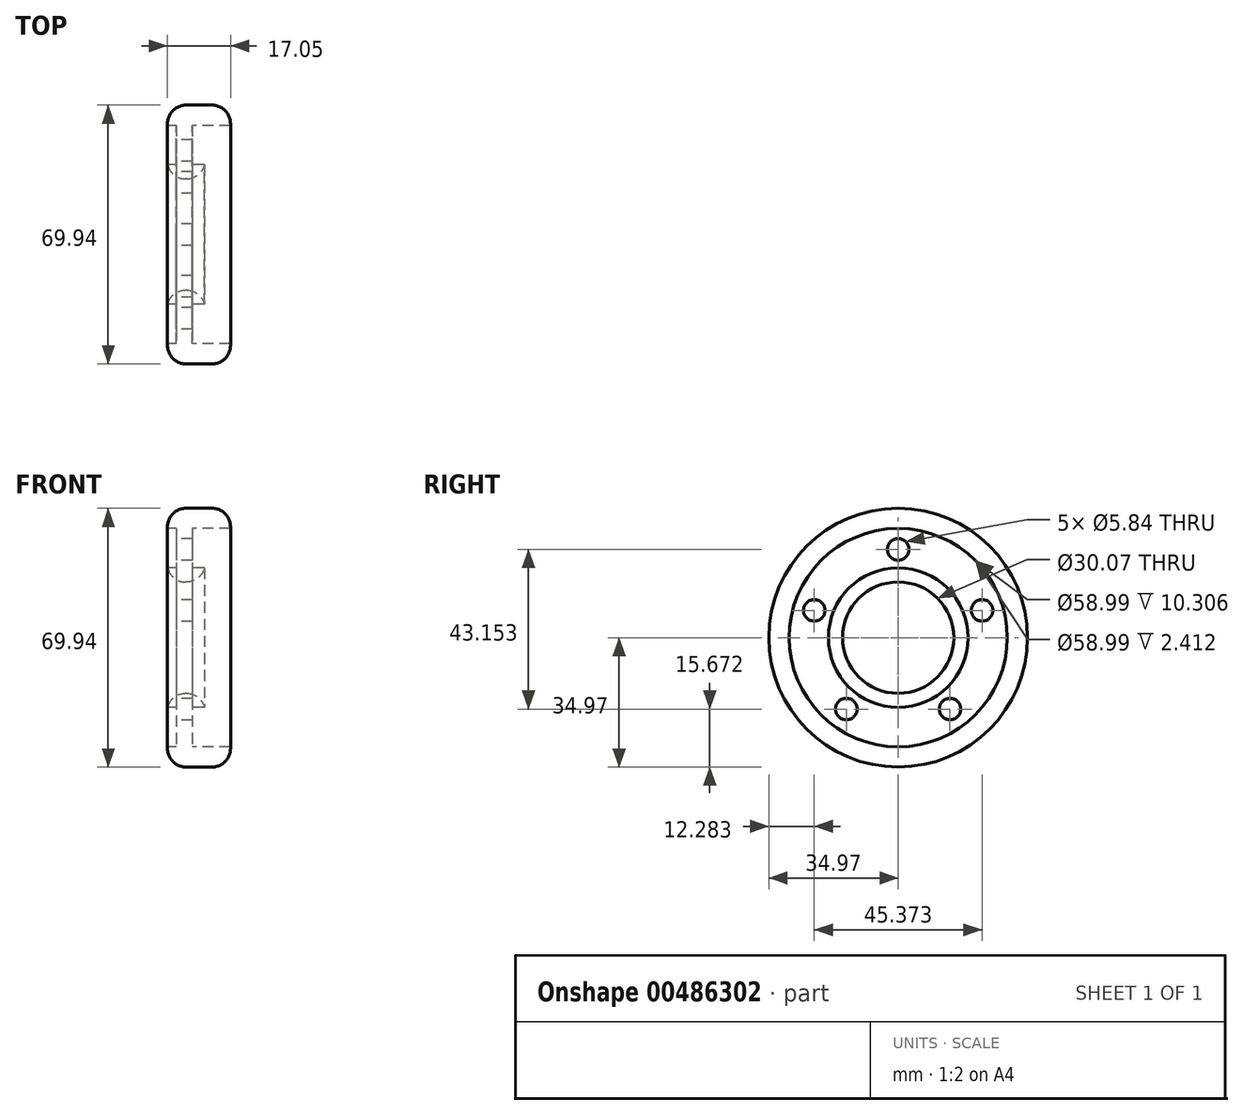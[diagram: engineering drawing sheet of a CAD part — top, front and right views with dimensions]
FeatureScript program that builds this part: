
annotation { "Feature Type Name" : "Feature", "Feature Type Description" : "" }
export const myFeature = defineFeature(function(context is Context, id is Id, definition is map)
    precondition{}
    {
        {
            var Q0;
            Q0=qCreatedBy(makeId("Front.planeOp"),FACE);
            var sketch = newSketch(context, id + "F0", { "sketchPlane" : qUnion([Q0])});
            skLineSegment(sketch, "E0", {"start": v(0, 15.04) * mm, "end": v(10, 15.04) * mm});
            skLineSegment(sketch, "E1", {"start": v(10, 15.04) * mm, "end": v(10, 18.87) * mm});
            skLineSegment(sketch, "E2", {"start": v(10, 18.87) * mm, "end": v(6.75, 18.87) * mm});
            skLineSegment(sketch, "E3", {"start": v(6.75, 18.87) * mm, "end": v(6.75, 29.5) * mm});
            skLineSegment(sketch, "E4", {"start": v(6.75, 29.5) * mm, "end": v(17.05, 29.5) * mm});
            skLineSegment(sketch, "E5", {"start": v(17.05, 29.5) * mm, "end": v(17.05, 34.97) * mm});
            skLineSegment(sketch, "E6", {"start": v(17.05, 34.97) * mm, "end": v(0, 34.97) * mm});
            skLineSegment(sketch, "E7", {"start": v(0, 34.97) * mm, "end": v(0, 29.5) * mm});
            skLineSegment(sketch, "E8", {"start": v(0, 29.5) * mm, "end": v(2.41, 29.5) * mm});
            skLineSegment(sketch, "E9", {"start": v(2.41, 29.5) * mm, "end": v(2.41, 18.87) * mm});
            skLineSegment(sketch, "E10", {"start": v(2.41, 18.87) * mm, "end": v(0, 18.87) * mm});
            skLineSegment(sketch, "E11", {"start": v(0, 18.87) * mm, "end": v(0, 15.04) * mm});
            skLineSegment(sketch, "E12", {"start": v(0, 0) * mm, "end": v(12.67, 0) * mm});
            skSolve(sketch);
        }
        {
            var Q0;
            Q0=makeQuery(id+"F0.imprint","IMPRINT",FACE,{"disambiguationData":[TD([[makeQuery(id+"F0.imprint","IMPRINT",EDGE,{"derivedFrom":sQuery(id+"F0.wireOp",EDGE,"E0")}),1.0]])]});
            var Q1;
            Q1=sQuery(id+"F0.wireOp",EDGE,"E12");
            revolve(context, id + "F1", {"entities" : qUnion([Q0]), "axis" : qUnion([Q1]), "revolveType" : RevolveType.FULL});
        }
        {
            var Q0;
            Q0=makeQuery(id+"F1.opRevolve","SWEPT_FACE",FACE,{"disambiguationData":[OSD([sQuery(id+"F0.wireOp",EDGE,"E9")])]});
            var sketch = newSketch(context, id + "F2", { "sketchPlane" : qUnion([Q0])});
            skCircle(sketch, "E13", {"center": v(0, 23.85) * mm, "radius": 2.92 * mm});
            skCircle(sketch, "E14.1.0", {"center": v(-22.69, 7.37) * mm, "radius": 2.92 * mm});
            skCircle(sketch, "E14.2.0", {"center": v(-14.02, -19.3) * mm, "radius": 2.92 * mm});
            skCircle(sketch, "E14.3.0", {"center": v(14.02, -19.3) * mm, "radius": 2.92 * mm});
            skCircle(sketch, "E14.4.0", {"center": v(22.69, 7.37) * mm, "radius": 2.92 * mm});
            skPoint(sketch, "E14.center", {"position": v(0, 0) * mm});
            skSolve(sketch);
        }
        {
            var Q0;
            Q0=makeQuery(id+"F2.imprint","IMPRINT",FACE,{"disambiguationData":[TD([[makeQuery(id+"F2.imprint","IMPRINT",EDGE,{"derivedFrom":sQuery(id+"F2.wireOp",EDGE,"E14.1.0")}),1.0]])]});
            var Q1;
            Q1=makeQuery(id+"F2.imprint","IMPRINT",FACE,{"disambiguationData":[TD([[makeQuery(id+"F2.imprint","IMPRINT",EDGE,{"derivedFrom":sQuery(id+"F2.wireOp",EDGE,"E13")}),1.0]])]});
            var Q2;
            Q2=makeQuery(id+"F2.imprint","IMPRINT",FACE,{"disambiguationData":[TD([[makeQuery(id+"F2.imprint","IMPRINT",EDGE,{"derivedFrom":sQuery(id+"F2.wireOp",EDGE,"E14.4.0")}),1.0]])]});
            var Q3;
            Q3=makeQuery(id+"F2.imprint","IMPRINT",FACE,{"disambiguationData":[TD([[makeQuery(id+"F2.imprint","IMPRINT",EDGE,{"derivedFrom":sQuery(id+"F2.wireOp",EDGE,"E14.3.0")}),1.0]])]});
            var Q4;
            Q4=makeQuery(id+"F2.imprint","IMPRINT",FACE,{"disambiguationData":[TD([[makeQuery(id+"F2.imprint","IMPRINT",EDGE,{"derivedFrom":sQuery(id+"F2.wireOp",EDGE,"E14.2.0")}),1.0]])]});
            extrude(context, id + "F3", {"entities" : qUnion([Q0, Q1, Q2, Q3, Q4]), "operationType" : NewBodyOperationType.REMOVE, "oppositeDirection" : true, "depth" : 25 * mm});
        }
        {
            var Q0;
            Q0=makeQuery(id+"F1.opRevolve","SWEPT_EDGE",EDGE,{"disambiguationData":[OSD([sQuery(id+"F0.wireOp",EDGE,"E6"),sQuery(id+"F0.wireOp",EDGE,"E7")])]});
            var Q1;
            Q1=makeQuery(id+"F1.opRevolve","SWEPT_EDGE",EDGE,{"disambiguationData":[OSD([sQuery(id+"F0.wireOp",EDGE,"E0"),sQuery(id+"F0.wireOp",EDGE,"E11")])]});
            var Q2;
            Q2=makeQuery(id+"F1.opRevolve","SWEPT_EDGE",EDGE,{"disambiguationData":[OSD([sQuery(id+"F0.wireOp",EDGE,"E5"),sQuery(id+"F0.wireOp",EDGE,"E6")])]});
            var Q3;
            Q3=makeQuery(id+"F1.opRevolve","SWEPT_EDGE",EDGE,{"disambiguationData":[OSD([sQuery(id+"F0.wireOp",EDGE,"E0"),sQuery(id+"F0.wireOp",EDGE,"E1")])]});
            fillet(context, id + "F4", {"entities" : qUnion([Q0, Q1, Q2, Q3]), "radius" : 5 * mm, "tangentPropagation" : true, "allowEdgeOverflow" : false});
        }
    });
